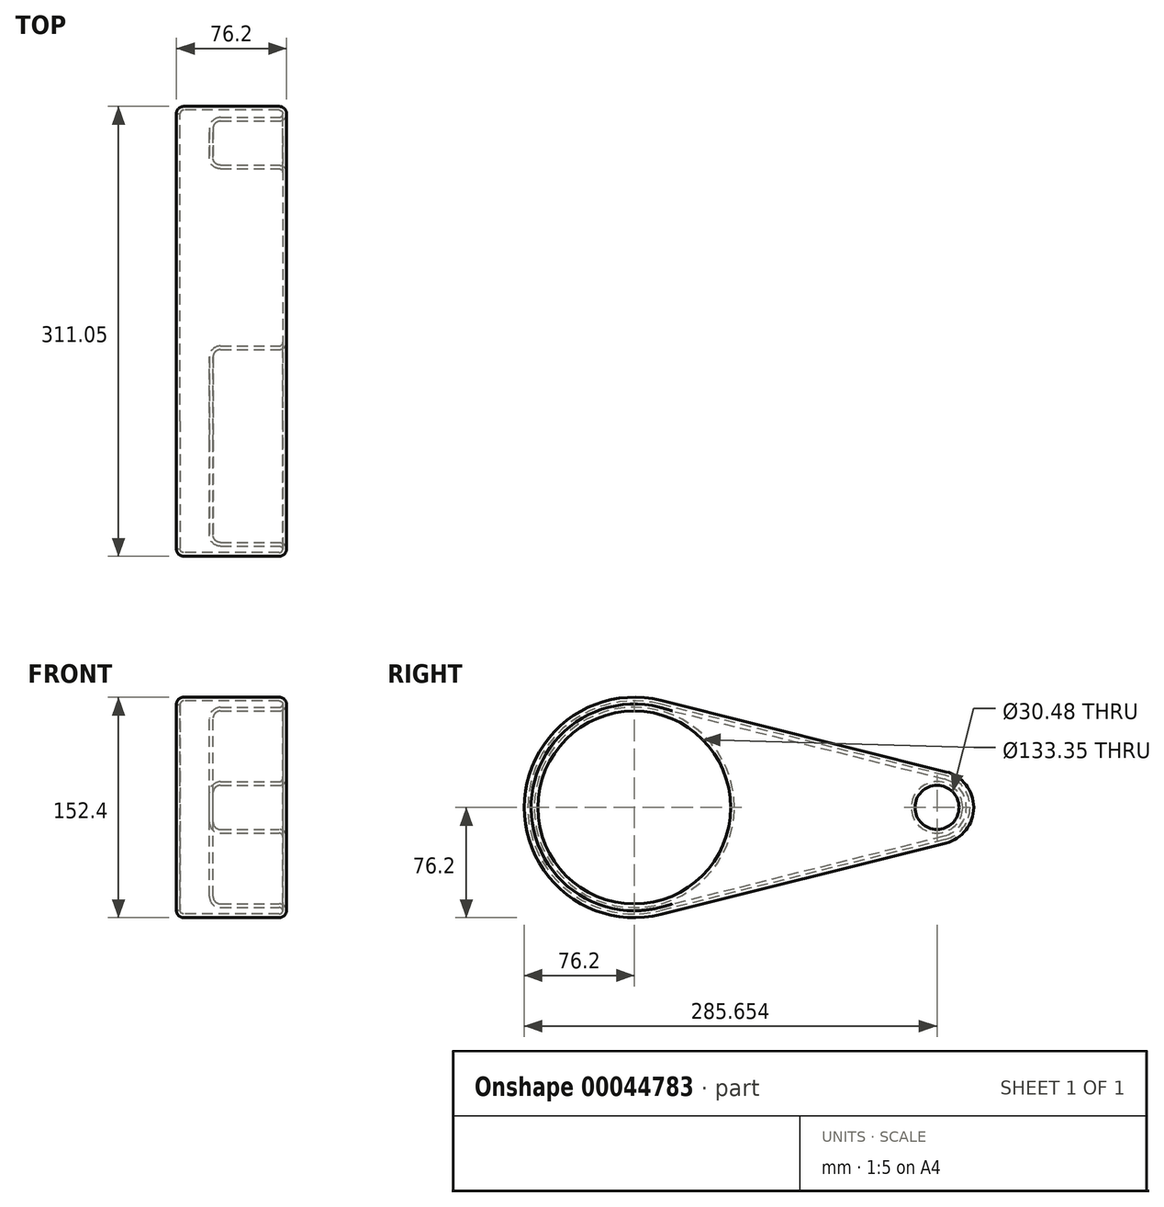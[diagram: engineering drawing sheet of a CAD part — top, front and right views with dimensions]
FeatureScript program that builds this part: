
annotation { "Feature Type Name" : "Feature", "Feature Type Description" : "" }
export const myFeature = defineFeature(function(context is Context, id is Id, definition is map)
    precondition{}
    {
        {
            var Q0;
            Q0=qCreatedBy(makeId("Right.planeOp"),FACE);
            var sketch = newSketch(context, id + "F0", { "sketchPlane" : qUnion([Q0])});
            skCircle(sketch, "E0", {"center": v(0, 0) * mm, "radius": 76.2 * mm});
            skCircle(sketch, "E1", {"center": v(209.45, 0) * mm, "radius": 25.4 * mm});
            skLineSegment(sketch, "E2", {"start": v(18.48, 73.92) * mm, "end": v(215.61, 24.64) * mm});
            skLineSegment(sketch, "E3", {"start": v(18.48, -73.92) * mm, "end": v(215.61, -24.64) * mm});
            skSolve(sketch);
        }
        {
            var Q0;
            Q0 = qSketchRegion(id + "F0", true);
            extrude(context, id + "F1", {"entities" : qUnion([Q0]), "depth" : 76.2 * mm});
        }
        {
            var Q0;
            Q0=makeQuery(id+"F1.opExtrude","CAP_FACE",FACE,{"disambiguationData":[OSD([sQuery(id+"F0.wireOp",EDGE,"E0"),sQuery(id+"F0.wireOp",EDGE,"E1"),sQuery(id+"F0.wireOp",EDGE,"E2"),sQuery(id+"F0.wireOp",EDGE,"E3")])],"isStart":false});
            var sketch = newSketch(context, id + "F2", { "sketchPlane" : qUnion([Q0])});
            skCircle(sketch, "E4", {"center": v(0, 0) * mm, "radius": 66.68 * mm});
            skCircle(sketch, "E5", {"center": v(209.45, 0) * mm, "radius": 15.24 * mm});
            skSolve(sketch);
        }
        {
            var Q0;
            Q0 = qSketchRegion(id + "F2", true);
            extrude(context, id + "F3", {"entities" : qUnion([Q0]), "operationType" : NewBodyOperationType.REMOVE, "oppositeDirection" : true, "depth" : 50.8 * mm});
        }
        {
            var Q0;
            Q0=makeQuery(id+"F1.opExtrude","CAP_FACE",FACE,{"disambiguationData":[OSD([sQuery(id+"F0.wireOp",EDGE,"E0"),sQuery(id+"F0.wireOp",EDGE,"E1"),sQuery(id+"F0.wireOp",EDGE,"E2"),sQuery(id+"F0.wireOp",EDGE,"E3")])],"isStart":false});
            var Q1;
            Q1=makeQuery(id+"F3.boolean.opBoolean","COPY",FACE,{"derivedFrom":makeQuery(id+"F3.opExtrude","CAP_FACE",FACE,{"disambiguationData":[OSD([sQuery(id+"F2.wireOp",EDGE,"E4")])],"isStart":false})});
            var Q2;
            Q2=makeQuery(id+"F3.boolean.opBoolean","COPY",FACE,{"derivedFrom":makeQuery(id+"F3.opExtrude","CAP_FACE",FACE,{"disambiguationData":[OSD([sQuery(id+"F2.wireOp",EDGE,"E5")])],"isStart":false})});
            var Q3;
            Q3=makeQuery(id+"F1.opExtrude","CAP_FACE",FACE,{"disambiguationData":[OSD([sQuery(id+"F0.wireOp",EDGE,"E0"),sQuery(id+"F0.wireOp",EDGE,"E1"),sQuery(id+"F0.wireOp",EDGE,"E2"),sQuery(id+"F0.wireOp",EDGE,"E3")])],"isStart":true});
            fillet(context, id + "F4", {"entities" : qUnion([Q0, Q1, Q2, Q3]), "radius" : 5.08 * mm, "tangentPropagation" : true, "allowEdgeOverflow" : false});
        }
        {
            var Q0;
            Q0=makeQuery(id+"F1.opExtrude","CAP_FACE",FACE,{"disambiguationData":[OSD([sQuery(id+"F0.wireOp",EDGE,"E0"),sQuery(id+"F0.wireOp",EDGE,"E1"),sQuery(id+"F0.wireOp",EDGE,"E2"),sQuery(id+"F0.wireOp",EDGE,"E3")])],"isStart":true});
            shell(context, id + "F5", {"entities" : qUnion([Q0]), "thickness" : 2.54 * mm});
        }
    });
